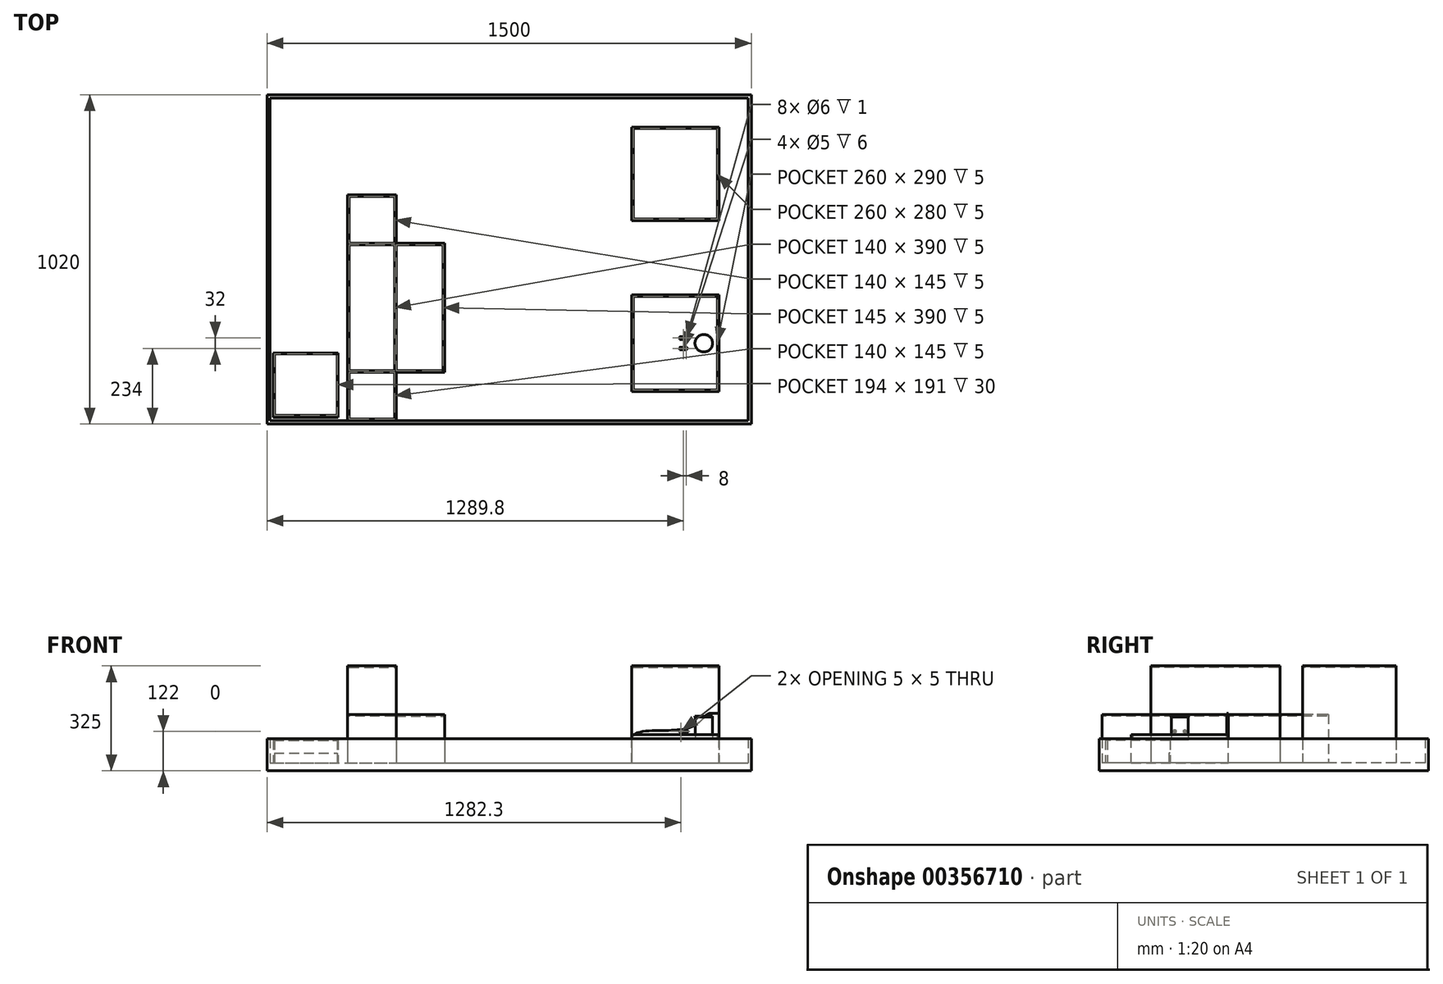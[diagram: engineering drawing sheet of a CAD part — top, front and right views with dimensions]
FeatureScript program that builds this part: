
annotation { "Feature Type Name" : "Feature", "Feature Type Description" : "" }
export const myFeature = defineFeature(function(context is Context, id is Id, definition is map)
    precondition{}
    {
        {
            var Q0;
            Q0=qCreatedBy(makeId("Top.planeOp"),FACE);
            var sketch = newSketch(context, id + "F0", { "sketchPlane" : qUnion([Q0])});
            skCircle(sketch, "E0", {"center": v(0, 0) * mm, "radius": 27.2 * mm});
            skSolve(sketch);
        }
        {
            var Q0;
            Q0=qSketchRegion(id+"F0",true);
            extrude(context, id + "F1", {"entities" : qUnion([Q0]), "depth" : 2.83 * mm});
        }
        {
            var Q0;
            Q0=makeQuery(id+"F1.opExtrude","CAP_FACE",FACE,{"disambiguationData":[OSD([sQuery(id+"F0.wireOp",EDGE,"E0")])],"isStart":false});
            var sketch = newSketch(context, id + "F2", { "sketchPlane" : qUnion([Q0])});
            skCircle(sketch, "E1", {"center": v(0, 0) * mm, "radius": 26.4 * mm});
            skSolve(sketch);
        }
        {
            var Q0;
            Q0=qSketchRegion(id+"F2",true);
            extrude(context, id + "F3", {"entities" : qUnion([Q0]), "operationType" : NewBodyOperationType.ADD, "depth" : 67.36 * mm});
        }
        {
            var Q0;
            Q0=makeQuery(id+"F3.opExtrude","CAP_FACE",FACE,{"disambiguationData":[OSD([sQuery(id+"F2.wireOp",EDGE,"E1")])],"isStart":false});
            var sketch = newSketch(context, id + "F4", { "sketchPlane" : qUnion([Q0])});
            skCircle(sketch, "E2", {"center": v(0, 0) * mm, "radius": 27.2 * mm});
            skSolve(sketch);
        }
        {
            var Q0;
            Q0=qSketchRegion(id+"F4",true);
            extrude(context, id + "F5", {"entities" : qUnion([Q0]), "operationType" : NewBodyOperationType.ADD, "depth" : 2.83 * mm});
        }
        {
            var Q0;
            Q0=makeQuery(id+"F5.opExtrude","CAP_FACE",FACE,{"disambiguationData":[OSD([sQuery(id+"F4.wireOp",EDGE,"E2")])],"isStart":false});
            var sketch = newSketch(context, id + "F6", { "sketchPlane" : qUnion([Q0])});
            skSolve(sketch);
        }
        {
            var Q0;
            Q0=qCreatedBy(makeId("Top.planeOp"),FACE);
            cPlane(context, id + "F7", {"entities" : qUnion([Q0]), "cplaneType" : CPlaneType.OFFSET, "offset" : 25 * mm, "width" : 150 * mm, "height" : 150 * mm});
        }
        {
            var Q0;
            Q0=makeQuery(id+"F6.imprint","IMPRINT",FACE,{"disambiguationData":[TD([[makeQuery(id+"F6.imprint","IMPRINT",EDGE,{"derivedFrom":makeQuery(id+"F5.opExtrude","CAP_EDGE",EDGE,{"disambiguationData":[OSD([sQuery(id+"F4.wireOp",EDGE,"E2")])],"isStart":false})}),1.0]])]});
            var sketch = newSketch(context, id + "F8", { "sketchPlane" : qUnion([Q0])});
            skSolve(sketch);
        }
        {
            var Q0;
            Q0=qCreatedBy(makeId("Top.planeOp"),FACE);
            var sketch = newSketch(context, id + "F9", { "sketchPlane" : qUnion([Q0])});
            skLineSegment(sketch, "E3.bottom", {"start": v(-222.8, -150) * mm, "end": v(47.2, -150) * mm});
            skLineSegment(sketch, "E3.top", {"start": v(-222.8, 150) * mm, "end": v(47.2, 150) * mm});
            skLineSegment(sketch, "E3.left", {"start": v(-222.8, -150) * mm, "end": v(-222.8, 150) * mm});
            skLineSegment(sketch, "E3.right", {"start": v(47.2, -150) * mm, "end": v(47.2, 150) * mm});
            skSolve(sketch);
        }
        {
            var Q0;
            Q0=qSketchRegion(id+"F9",true);
            extrude(context, id + "F10", {"entities" : qUnion([Q0]), "oppositeDirection" : true, "depth" : 72 * mm});
        }
        {
            var Q0;
            Q0=makeQuery(id+"F10.opExtrude","CAP_FACE",FACE,{"disambiguationData":[OSD([sQuery(id+"F9.wireOp",EDGE,"E3.bottom"),sQuery(id+"F9.wireOp",EDGE,"E3.top"),sQuery(id+"F9.wireOp",EDGE,"E3.left"),sQuery(id+"F9.wireOp",EDGE,"E3.right")])],"isStart":true});
            var sketch = newSketch(context, id + "F11", { "sketchPlane" : qUnion([Q0])});
            skLineSegment(sketch, "E4.bottom", {"start": v(-222.8, -150) * mm, "end": v(47.2, -150) * mm});
            skLineSegment(sketch, "E4.top", {"start": v(-222.8, -145) * mm, "end": v(42.2, -145) * mm});
            skLineSegment(sketch, "E4.left", {"start": v(-222.8, -150) * mm, "end": v(-222.8, -145) * mm});
            skLineSegment(sketch, "E5.bottom", {"start": v(47.2, 150) * mm, "end": v(42.2, 150) * mm});
            skLineSegment(sketch, "E5.left", {"start": v(47.2, 150) * mm, "end": v(47.2, -150) * mm});
            skLineSegment(sketch, "E5.right", {"start": v(42.2, 150) * mm, "end": v(42.2, -145) * mm});
            skSolve(sketch);
        }
        {
            var Q0;
            Q0=qSketchRegion(id+"F11",true);
            extrude(context, id + "F12", {"entities" : qUnion([Q0]), "operationType" : NewBodyOperationType.ADD, "depth" : 15 * mm});
        }
        {
            var Q0;
            Q0=makeQuery(id+"F12.boolean.opBoolean","MERGE",FACE,{"derivedFrom":[makeQuery(id+"F10.opExtrude","SWEPT_FACE",FACE,{"disambiguationData":[OSD([sQuery(id+"F9.wireOp",EDGE,"E3.top")])]}),makeQuery(id+"F12.opExtrude","SWEPT_FACE",FACE,{"disambiguationData":[OSD([sQuery(id+"F11.wireOp",EDGE,"E5.bottom")])]})]});
            var sketch = newSketch(context, id + "F13", { "sketchPlane" : qUnion([Q0])});
            skLineSegment(sketch, "E6", {"start": v(-47.2, 81.36) * mm, "end": v(-21.31, 81.36) * mm});
            skFitSpline(sketch, "E7", {"points": [v(-21.31, 81.36) * mm, v(15.24, 52.01) * mm, v(114.14, 28.17) * mm, v(222.8, 0) * mm], "startDerivative": vector(181.02, 0.3) * mm, "endDerivative": vector(-1.73, -239.85) * mm});
            skLineSegment(sketch, "E8", {"start": v(-47.2, 81.36) * mm, "end": v(-47.2, -72) * mm});
            skLineSegment(sketch, "E9", {"start": v(-47.2, -72) * mm, "end": v(222.8, -72) * mm});
            skLineSegment(sketch, "E10", {"start": v(222.8, -72) * mm, "end": v(222.8, 0) * mm});
            skSolve(sketch);
        }
        {
            var Q0;
            Q0=qSketchRegion(id+"F13",true);
            extrude(context, id + "F14", {"entities" : qUnion([Q0]), "operationType" : NewBodyOperationType.ADD, "oppositeDirection" : true, "depth" : 5 * mm});
        }
        {
            var Q0;
            Q0=makeQuery(id+"F10.opExtrude","CAP_FACE",FACE,{"disambiguationData":[OSD([sQuery(id+"F9.wireOp",EDGE,"E3.bottom"),sQuery(id+"F9.wireOp",EDGE,"E3.top"),sQuery(id+"F9.wireOp",EDGE,"E3.left"),sQuery(id+"F9.wireOp",EDGE,"E3.right")])],"isStart":true});
            var sketch = newSketch(context, id + "F15", { "sketchPlane" : qUnion([Q0])});
            skLineSegment(sketch, "E11.bottom", {"start": v(-222.8, 145) * mm, "end": v(-217.8, 145) * mm});
            skLineSegment(sketch, "E11.top", {"start": v(-222.8, -145) * mm, "end": v(-217.8, -145) * mm});
            skLineSegment(sketch, "E11.left", {"start": v(-222.8, 145) * mm, "end": v(-222.8, -145) * mm});
            skLineSegment(sketch, "E11.right", {"start": v(-217.8, 145) * mm, "end": v(-217.8, -145) * mm});
            skSolve(sketch);
        }
        {
            var Q0;
            Q0=qSketchRegion(id+"F15",true);
            extrude(context, id + "F16", {"entities" : qUnion([Q0]), "operationType" : NewBodyOperationType.ADD, "depth" : 5 * mm});
        }
        {
            var Q0;
            Q0=makeQuery(id+"F10.opExtrude","CAP_FACE",FACE,{"disambiguationData":[OSD([sQuery(id+"F9.wireOp",EDGE,"E3.bottom"),sQuery(id+"F9.wireOp",EDGE,"E3.top"),sQuery(id+"F9.wireOp",EDGE,"E3.left"),sQuery(id+"F9.wireOp",EDGE,"E3.right")])],"isStart":false});
            var sketch = newSketch(context, id + "F17", { "sketchPlane" : qUnion([Q0])});
            skLineSegment(sketch, "E12.bottom", {"start": v(147.2, 250) * mm, "end": v(-1352.8, 250) * mm});
            skLineSegment(sketch, "E12.top", {"start": v(147.2, -770) * mm, "end": v(-1352.8, -770) * mm});
            skLineSegment(sketch, "E12.left", {"start": v(147.2, 250) * mm, "end": v(147.2, -770) * mm});
            skLineSegment(sketch, "E12.right", {"start": v(-1352.8, 250) * mm, "end": v(-1352.8, -770) * mm});
            skSolve(sketch);
        }
        {
            var Q0;
            Q0=qSketchRegion(id+"F17",true);
            extrude(context, id + "F18", {"entities" : qUnion([Q0]), "operationType" : NewBodyOperationType.ADD, "depth" : 25 * mm});
        }
        {
            var Q0;
            Q0=makeQuery(id+"F18.opExtrude","CAP_FACE",FACE,{"disambiguationData":[OSD([sQuery(id+"F17.wireOp",EDGE,"E12.bottom"),sQuery(id+"F17.wireOp",EDGE,"E12.top"),sQuery(id+"F17.wireOp",EDGE,"E12.left"),sQuery(id+"F17.wireOp",EDGE,"E12.right")])],"isStart":true});
            var sketch = newSketch(context, id + "F19", { "sketchPlane" : qUnion([Q0])});
            skLineSegment(sketch, "E13.bottom", {"start": v(-222.8, 670) * mm, "end": v(47.2, 670) * mm});
            skLineSegment(sketch, "E13.top", {"start": v(-222.8, 380) * mm, "end": v(47.2, 380) * mm});
            skLineSegment(sketch, "E13.left", {"start": v(-222.8, 670) * mm, "end": v(-222.8, 380) * mm});
            skLineSegment(sketch, "E13.right", {"start": v(47.2, 670) * mm, "end": v(47.2, 380) * mm});
            skSolve(sketch);
        }
        {
            var Q0;
            Q0=qSketchRegion(id+"F19",true);
            extrude(context, id + "F20", {"entities" : qUnion([Q0]), "operationType" : NewBodyOperationType.ADD, "depth" : 300 * mm});
        }
        {
            var Q0;
            Q0=makeQuery(id+"F20.opExtrude","CAP_FACE",FACE,{"disambiguationData":[OSD([sQuery(id+"F19.wireOp",EDGE,"E13.bottom"),sQuery(id+"F19.wireOp",EDGE,"E13.top"),sQuery(id+"F19.wireOp",EDGE,"E13.left"),sQuery(id+"F19.wireOp",EDGE,"E13.right")])],"isStart":false});
            var sketch = newSketch(context, id + "F21", { "sketchPlane" : qUnion([Q0])});
            skLineSegment(sketch, "E14.bottom", {"start": v(-217.8, 665) * mm, "end": v(42.2, 665) * mm});
            skLineSegment(sketch, "E14.top", {"start": v(-217.8, 385) * mm, "end": v(42.2, 385) * mm});
            skLineSegment(sketch, "E14.left", {"start": v(-217.8, 665) * mm, "end": v(-217.8, 385) * mm});
            skLineSegment(sketch, "E14.right", {"start": v(42.2, 665) * mm, "end": v(42.2, 385) * mm});
            skSolve(sketch);
        }
        {
            var Q0;
            Q0=qSketchRegion(id+"F21",true);
            extrude(context, id + "F22", {"entities" : qUnion([Q0]), "operationType" : NewBodyOperationType.REMOVE, "oppositeDirection" : true, "depth" : 5 * mm});
        }
        {
            var Q0;
            Q0=makeQuery(id+"F18.opExtrude","CAP_FACE",FACE,{"disambiguationData":[OSD([sQuery(id+"F17.wireOp",EDGE,"E12.bottom"),sQuery(id+"F17.wireOp",EDGE,"E12.top"),sQuery(id+"F17.wireOp",EDGE,"E12.left"),sQuery(id+"F17.wireOp",EDGE,"E12.right")])],"isStart":true});
            var sketch = newSketch(context, id + "F23", { "sketchPlane" : qUnion([Q0])});
            skLineSegment(sketch, "E15.bottom", {"start": v(-1352.8, 770) * mm, "end": v(147.2, 770) * mm});
            skLineSegment(sketch, "E15.top", {"start": v(-1352.8, -250) * mm, "end": v(147.2, -250) * mm});
            skLineSegment(sketch, "E15.left", {"start": v(-1352.8, 770) * mm, "end": v(-1352.8, -250) * mm});
            skLineSegment(sketch, "E15.right", {"start": v(147.2, 770) * mm, "end": v(147.2, -250) * mm});
            skLineSegment(sketch, "E16.bottom", {"start": v(-1342.8, 760) * mm, "end": v(137.2, 760) * mm});
            skLineSegment(sketch, "E16.top", {"start": v(-1342.8, -240) * mm, "end": v(137.2, -240) * mm});
            skLineSegment(sketch, "E16.left", {"start": v(-1342.8, 760) * mm, "end": v(-1342.8, -240) * mm});
            skLineSegment(sketch, "E16.right", {"start": v(137.2, 760) * mm, "end": v(137.2, -240) * mm});
            skSolve(sketch);
        }
        {
            var Q0;
            Q0=qSketchRegion(id+"F23",true);
            extrude(context, id + "F24", {"entities" : qUnion([Q0]), "operationType" : NewBodyOperationType.ADD, "depth" : 75 * mm});
        }
        {
            var Q0;
            Q0=makeQuery(id+"F18.opExtrude","CAP_FACE",FACE,{"disambiguationData":[OSD([sQuery(id+"F17.wireOp",EDGE,"E12.bottom"),sQuery(id+"F17.wireOp",EDGE,"E12.top"),sQuery(id+"F17.wireOp",EDGE,"E12.left"),sQuery(id+"F17.wireOp",EDGE,"E12.right")])],"isStart":true});
            var sketch = newSketch(context, id + "F25", { "sketchPlane" : qUnion([Q0])});
            skLineSegment(sketch, "E17.bottom", {"start": v(-1102.8, 460) * mm, "end": v(-952.8, 460) * mm});
            skLineSegment(sketch, "E17.top", {"start": v(-1102.8, -240) * mm, "end": v(-952.8, -240) * mm});
            skLineSegment(sketch, "E17.left", {"start": v(-1102.8, 460) * mm, "end": v(-1102.8, -240) * mm});
            skLineSegment(sketch, "E17.right", {"start": v(-952.8, 460) * mm, "end": v(-952.8, 310) * mm});
            skLineSegment(sketch, "E18.bottom", {"start": v(-952.8, 310) * mm, "end": v(-802.8, 310) * mm});
            skLineSegment(sketch, "E18.top", {"start": v(-952.8, -90) * mm, "end": v(-802.8, -90) * mm});
            skLineSegment(sketch, "E18.right", {"start": v(-802.8, 310) * mm, "end": v(-802.8, -90) * mm});
            skLineSegment(sketch, "E19.trimOffspring", {"start": v(-952.8, -90) * mm, "end": v(-952.8, -240) * mm});
            skSolve(sketch);
        }
        {
            var Q0;
            Q0=qSketchRegion(id+"F25",true);
            extrude(context, id + "F26", {"entities" : qUnion([Q0]), "operationType" : NewBodyOperationType.ADD, "depth" : 150 * mm});
        }
        {
            var Q0;
            Q0=makeQuery(id+"F26.opExtrude","CAP_FACE",FACE,{"disambiguationData":[OSD([sQuery(id+"F25.wireOp",EDGE,"E17.bottom"),sQuery(id+"F25.wireOp",EDGE,"E17.top"),sQuery(id+"F25.wireOp",EDGE,"E17.left"),sQuery(id+"F25.wireOp",EDGE,"E17.right"),sQuery(id+"F25.wireOp",EDGE,"E18.bottom"),sQuery(id+"F25.wireOp",EDGE,"E18.top"),sQuery(id+"F25.wireOp",EDGE,"E18.right"),sQuery(id+"F25.wireOp",EDGE,"E19.trimOffspring")])],"isStart":false});
            var sketch = newSketch(context, id + "F27", { "sketchPlane" : qUnion([Q0])});
            skLineSegment(sketch, "E20.bottom", {"start": v(-952.8, 310) * mm, "end": v(-1102.8, 310) * mm});
            skLineSegment(sketch, "E20.top", {"start": v(-952.8, -90) * mm, "end": v(-1102.8, -90) * mm});
            skLineSegment(sketch, "E20.left", {"start": v(-952.8, 310) * mm, "end": v(-952.8, -90) * mm});
            skLineSegment(sketch, "E20.right", {"start": v(-1102.8, 310) * mm, "end": v(-1102.8, -90) * mm});
            skSolve(sketch);
        }
        {
            var Q0;
            Q0=qSketchRegion(id+"F27",true);
            extrude(context, id + "F28", {"entities" : qUnion([Q0]), "operationType" : NewBodyOperationType.ADD, "depth" : 150 * mm});
        }
        {
            var Q0;
            Q0=makeQuery(id+"F28.opExtrude","CAP_FACE",FACE,{"disambiguationData":[OSD([sQuery(id+"F27.wireOp",EDGE,"E20.bottom"),sQuery(id+"F27.wireOp",EDGE,"E20.top"),sQuery(id+"F27.wireOp",EDGE,"E20.left"),sQuery(id+"F27.wireOp",EDGE,"E20.right")])],"isStart":false});
            var sketch = newSketch(context, id + "F29", { "sketchPlane" : qUnion([Q0])});
            skLineSegment(sketch, "E21.bottom", {"start": v(-1097.8, 305) * mm, "end": v(-957.8, 305) * mm});
            skLineSegment(sketch, "E21.top", {"start": v(-1097.8, -85) * mm, "end": v(-957.8, -85) * mm});
            skLineSegment(sketch, "E21.left", {"start": v(-1097.8, 305) * mm, "end": v(-1097.8, -85) * mm});
            skLineSegment(sketch, "E21.right", {"start": v(-957.8, 305) * mm, "end": v(-957.8, -85) * mm});
            skSolve(sketch);
        }
        {
            var Q0;
            Q0=qSketchRegion(id+"F29",true);
            extrude(context, id + "F30", {"entities" : qUnion([Q0]), "operationType" : NewBodyOperationType.REMOVE, "oppositeDirection" : true, "depth" : 5 * mm});
        }
        {
            var Q0;
            {var subQ0=sQuery(id+"F25.wireOp",EDGE,"E17.left");var subQ1=sQuery(id+"F25.wireOp",EDGE,"E18.bottom");var subQ2=sQuery(id+"F25.wireOp",EDGE,"E17.right");var subQ3=sQuery(id+"F25.wireOp",EDGE,"E17.bottom");var subQ4=makeQuery(id+"F26.opExtrude","CAP_FACE",FACE,{"disambiguationData":[OSD([subQ3,sQuery(id+"F25.wireOp",EDGE,"E17.top"),subQ0,subQ2,subQ1,sQuery(id+"F25.wireOp",EDGE,"E18.top"),sQuery(id+"F25.wireOp",EDGE,"E18.right"),sQuery(id+"F25.wireOp",EDGE,"E19.trimOffspring")])],"isStart":false});Q0=makeQuery(id+"F28.boolean.opBoolean","SPLIT",FACE,{"disambiguationData":[TD([makeQuery(id+"F26.opExtrude","SWEPT_FACE",FACE,{"disambiguationData":[OSD([subQ3])]})])],"derivedFrom":subQ4});}
            var sketch = newSketch(context, id + "F31", { "sketchPlane" : qUnion([Q0])});
            skLineSegment(sketch, "E22.bottom", {"start": v(-1097.8, 455) * mm, "end": v(-957.8, 455) * mm});
            skLineSegment(sketch, "E22.top", {"start": v(-1097.8, 310) * mm, "end": v(-957.8, 310) * mm});
            skLineSegment(sketch, "E22.left", {"start": v(-1097.8, 455) * mm, "end": v(-1097.8, 310) * mm});
            skLineSegment(sketch, "E22.right", {"start": v(-957.8, 455) * mm, "end": v(-957.8, 310) * mm});
            skLineSegment(sketch, "E23.bottom", {"start": v(-952.8, 305) * mm, "end": v(-807.8, 305) * mm});
            skLineSegment(sketch, "E23.top", {"start": v(-952.8, -85) * mm, "end": v(-807.8, -85) * mm});
            skLineSegment(sketch, "E23.left", {"start": v(-952.8, 305) * mm, "end": v(-952.8, -85) * mm});
            skLineSegment(sketch, "E23.right", {"start": v(-807.8, 305) * mm, "end": v(-807.8, -85) * mm});
            skLineSegment(sketch, "E24.bottom", {"start": v(-1097.8, -90) * mm, "end": v(-957.8, -90) * mm});
            skLineSegment(sketch, "E24.top", {"start": v(-1097.8, -235) * mm, "end": v(-957.8, -235) * mm});
            skLineSegment(sketch, "E24.left", {"start": v(-1097.8, -90) * mm, "end": v(-1097.8, -235) * mm});
            skLineSegment(sketch, "E24.right", {"start": v(-957.8, -90) * mm, "end": v(-957.8, -235) * mm});
            skSolve(sketch);
        }
        {
            var Q0;
            Q0=qSketchRegion(id+"F31",true);
            extrude(context, id + "F32", {"entities" : qUnion([Q0]), "operationType" : NewBodyOperationType.REMOVE, "oppositeDirection" : true, "depth" : 5 * mm});
        }
        {
            var Q0;
            Q0=qCreatedBy(id+"F7.planeOp",FACE);
            var sketch = newSketch(context, id + "F33", { "sketchPlane" : qUnion([Q0])});
            skLineSegment(sketch, "E25", {"start": v(0, 0) * mm, "end": v(-90, 0) * mm, "construction": true});
            skLineSegment(sketch, "E26.bottom", {"start": v(-74.5, -12) * mm, "end": v(-55, -12) * mm});
            skLineSegment(sketch, "E26.top", {"start": v(-74.5, -20) * mm, "end": v(-55, -20) * mm});
            skLineSegment(sketch, "E26.left", {"start": v(-74.5, -12) * mm, "end": v(-74.5, -13) * mm});
            skPoint(sketch, "E27.visualSharp", {"position": v(-51, -12) * mm});
            skPoint(sketch, "E28.visualSharp", {"position": v(-51, -20) * mm});
            skCircle(sketch, "E29", {"center": v(-55, -16) * mm, "radius": 3 * mm});
            skLineSegment(sketch, "E30", {"start": v(-59, -3.98) * mm, "end": v(-59, -18.08) * mm, "construction": true});
            skCircle(sketch, "E31.MirrorC", {"center": v(-63, -16) * mm, "radius": 3 * mm});
            skLineSegment(sketch, "E32.bottom", {"start": v(-74.5, -13) * mm, "end": v(-65.65, -13) * mm});
            skLineSegment(sketch, "E32.top", {"start": v(-74.5, -19) * mm, "end": v(-65.65, -19) * mm});
            skArc(sketch, "E33", {"start": v(-65.65, -13) * mm, "mid": v(-67, -16) * mm, "end": v(-65.65, -19) * mm});
            skLineSegment(sketch, "E34.trimOffspring", {"start": v(-74.5, -19) * mm, "end": v(-74.5, -20) * mm});
            skArc(sketch, "E35.trimOffspring", {"start": v(-55, -20) * mm, "mid": v(-51, -16) * mm, "end": v(-55, -12) * mm});
            skLineSegment(sketch, "E36.MirrorCS", {"start": v(-74.5, 12) * mm, "end": v(-74.5, 13) * mm});
            skLineSegment(sketch, "E37.MirrorCS", {"start": v(-74.5, 19) * mm, "end": v(-74.5, 20) * mm});
            skPoint(sketch, "E38.MirrorP", {"position": v(-51, 12) * mm});
            skLineSegment(sketch, "E39.MirrorCS", {"start": v(-74.5, 12) * mm, "end": v(-55, 12) * mm});
            skPoint(sketch, "E40.MirrorP", {"position": v(-51, 20) * mm});
            skArc(sketch, "E41.MirrorCS", {"start": v(-65.65, 13) * mm, "mid": v(-67, 16) * mm, "end": v(-65.65, 19) * mm});
            skArc(sketch, "E42.MirrorCS", {"start": v(-55, 20) * mm, "mid": v(-51, 16) * mm, "end": v(-55, 12) * mm});
            skLineSegment(sketch, "E43.MirrorCS", {"start": v(-74.5, 20) * mm, "end": v(-55, 20) * mm});
            skCircle(sketch, "E44.MirrorC", {"center": v(-55, 16) * mm, "radius": 3 * mm});
            skCircle(sketch, "E45.MirrorC", {"center": v(-63, 16) * mm, "radius": 3 * mm});
            skLineSegment(sketch, "E46.MirrorCS", {"start": v(-74.5, 19) * mm, "end": v(-65.65, 19) * mm});
            skLineSegment(sketch, "E47.MirrorCS", {"start": v(-74.5, 13) * mm, "end": v(-65.65, 13) * mm});
            skSolve(sketch);
        }
        {
            var Q0;
            Q0=qSketchRegion(id+"F33",true);
            var Q1;
            Q1=qSketchRegion(id+"F36",true);
            extrude(context, id + "F34", {"entities" : qUnion([Q0, Q1]), "depth" : 8 * mm, "symmetric" : true});
        }
        {
            var Q0;
            Q0=makeQuery(id+"F34.opExtrude","CAP_EDGE",EDGE,{"disambiguationData":[OSD([sQuery(id+"F33.wireOp",EDGE,"E34.trimOffspring")])],"isStart":false});
            var Q1;
            Q1=makeQuery(id+"F34.opExtrude","CAP_EDGE",EDGE,{"disambiguationData":[OSD([sQuery(id+"F33.wireOp",EDGE,"E26.left")])],"isStart":false});
            var Q2;
            Q2=makeQuery(id+"F34.opExtrude","CAP_EDGE",EDGE,{"disambiguationData":[OSD([sQuery(id+"F33.wireOp",EDGE,"E34.trimOffspring")])],"isStart":true});
            var Q3;
            Q3=makeQuery(id+"F34.opExtrude","CAP_EDGE",EDGE,{"disambiguationData":[OSD([sQuery(id+"F33.wireOp",EDGE,"E26.left")])],"isStart":true});
            var Q4;
            Q4=makeQuery(id+"F34.opExtrude","CAP_EDGE",EDGE,{"disambiguationData":[OSD([sQuery(id+"F33.wireOp",EDGE,"E36.MirrorCS")])],"isStart":false});
            var Q5;
            Q5=makeQuery(id+"F34.opExtrude","CAP_EDGE",EDGE,{"disambiguationData":[OSD([sQuery(id+"F33.wireOp",EDGE,"E37.MirrorCS")])],"isStart":false});
            var Q6;
            Q6=makeQuery(id+"F34.opExtrude","CAP_EDGE",EDGE,{"disambiguationData":[OSD([sQuery(id+"F33.wireOp",EDGE,"E37.MirrorCS")])],"isStart":true});
            var Q7;
            Q7=makeQuery(id+"F34.opExtrude","CAP_EDGE",EDGE,{"disambiguationData":[OSD([sQuery(id+"F33.wireOp",EDGE,"E36.MirrorCS")])],"isStart":true});
            fillet(context, id + "F35", {"entities" : qUnion([Q0, Q1, Q2, Q3, Q4, Q5, Q6, Q7]), "radius" : 4 * mm, "tangentPropagation" : true, "allowEdgeOverflow" : false});
        }
        {
            var Q0;
            Q0=makeQuery(id+"F34.opExtrude","SWEPT_FACE",FACE,{"disambiguationData":[OSD([sQuery(id+"F33.wireOp",EDGE,"E26.top")])]});
            var sketch = newSketch(context, id + "F36", { "sketchPlane" : qUnion([Q0])});
            skCircle(sketch, "E48", {"center": v(-70.5, 25) * mm, "radius": 3 * mm});
            skSolve(sketch);
        }
        {
            var Q0;
            Q0=qSketchRegion(id+"F36",true);
            var Q1;
            Q1=makeQuery(id+"F34.opExtrude","SWEPT_FACE",FACE,{"disambiguationData":[OSD([sQuery(id+"F33.wireOp",EDGE,"E26.bottom")])]});
            extrude(context, id + "F37", {"entities" : qUnion([Q0]), "operationType" : NewBodyOperationType.ADD, "endBound" : BoundingType.UP_TO_SURFACE, "oppositeDirection" : true, "endBoundEntityFace" : qUnion([Q1]), "depth" : 25 * mm});
        }
        {
            var Q0;
            Q0=makeQuery(id+"F34.opExtrude","SWEPT_FACE",FACE,{"disambiguationData":[OSD([sQuery(id+"F33.wireOp",EDGE,"E43.MirrorCS")])]});
            var sketch = newSketch(context, id + "F38", { "sketchPlane" : qUnion([Q0])});
            skCircle(sketch, "E49", {"center": v(70.5, 25) * mm, "radius": 3 * mm});
            skSolve(sketch);
        }
        {
            var Q0;
            Q0=qSketchRegion(id+"F38",true);
            var Q1;
            Q1=makeQuery(id+"F34.opExtrude","SWEPT_FACE",FACE,{"disambiguationData":[OSD([sQuery(id+"F33.wireOp",EDGE,"E39.MirrorCS")])]});
            extrude(context, id + "F39", {"entities" : qUnion([Q0]), "operationType" : NewBodyOperationType.ADD, "endBound" : BoundingType.UP_TO_SURFACE, "oppositeDirection" : true, "endBoundEntityFace" : qUnion([Q1]), "depth" : 25 * mm});
        }
        {
            var Q0;
            Q0=qCreatedBy(id+"F7.planeOp",FACE);
            var sketch = newSketch(context, id + "F40", { "sketchPlane" : qUnion([Q0])});
            skCircle(sketch, "E50", {"center": v(-55, 16) * mm, "radius": 3 * mm});
            skCircle(sketch, "E51", {"center": v(-63, 16) * mm, "radius": 2.5 * mm});
            skCircle(sketch, "E52", {"center": v(-63, 16) * mm, "radius": 3 * mm});
            skCircle(sketch, "E53", {"center": v(-55, 16) * mm, "radius": 2.5 * mm});
            skSolve(sketch);
        }
        {
            var Q0;
            Q0=qSketchRegion(id+"F40",true);
            extrude(context, id + "F41", {"entities" : qUnion([Q0]), "operationType" : NewBodyOperationType.ADD, "depth" : 6 * mm, "symmetric" : true});
        }
        {
            var Q0;
            Q0=qCreatedBy(id+"F7.planeOp",FACE);
            var sketch = newSketch(context, id + "F42", { "sketchPlane" : qUnion([Q0])});
            skCircle(sketch, "E54", {"center": v(-63, -16) * mm, "radius": 2.5 * mm});
            skCircle(sketch, "E55", {"center": v(-63, -16) * mm, "radius": 3 * mm});
            skCircle(sketch, "E56", {"center": v(-55, -16) * mm, "radius": 2.5 * mm});
            skCircle(sketch, "E57", {"center": v(-55, -16) * mm, "radius": 3 * mm});
            skSolve(sketch);
        }
        {
            var Q0;
            Q0=qSketchRegion(id+"F42",true);
            extrude(context, id + "F43", {"entities" : qUnion([Q0]), "operationType" : NewBodyOperationType.ADD, "depth" : 6 * mm, "symmetric" : true});
        }
        {
            var Q0;
            Q0=makeQuery(id+"F34.opExtrude","SWEPT_FACE",FACE,{"disambiguationData":[OSD([sQuery(id+"F33.wireOp",EDGE,"E43.MirrorCS")])]});
            var sketch = newSketch(context, id + "F44", { "sketchPlane" : qUnion([Q0])});
            skArc(sketch, "E58", {"start": v(71.5, 27.3) * mm, "mid": v(70.5, 27.5) * mm, "end": v(69.5, 27.3) * mm});
            skLineSegment(sketch, "E59.bottom", {"start": v(68.2, 26) * mm, "end": v(69.5, 26) * mm});
            skLineSegment(sketch, "E59.top", {"start": v(68.2, 24) * mm, "end": v(69.5, 24) * mm});
            skLineSegment(sketch, "E60.left", {"start": v(71.5, 27.3) * mm, "end": v(71.5, 26) * mm});
            skLineSegment(sketch, "E60.right", {"start": v(69.5, 27.3) * mm, "end": v(69.5, 26) * mm});
            skPoint(sketch, "E61.orphan", {"position": v(69.5, 27.8) * mm});
            skPoint(sketch, "E62.orphan", {"position": v(71.5, 27.8) * mm});
            skArc(sketch, "E63.trimOffspring", {"start": v(68.2, 26) * mm, "mid": v(68, 25) * mm, "end": v(68.2, 24) * mm});
            skPoint(sketch, "E59.left.start.orphan", {"position": v(67.32, 26) * mm});
            skPoint(sketch, "E64.orphan", {"position": v(67.32, 24) * mm});
            skArc(sketch, "E65.trimOffspring", {"start": v(69.5, 22.7) * mm, "mid": v(70.5, 22.5) * mm, "end": v(71.5, 22.7) * mm});
            skLineSegment(sketch, "E66.trimOffspring", {"start": v(69.5, 24) * mm, "end": v(69.5, 22.7) * mm});
            skLineSegment(sketch, "E67.trimOffspring", {"start": v(71.5, 26) * mm, "end": v(72.8, 26) * mm});
            skLineSegment(sketch, "E68.trimOffspring", {"start": v(71.5, 24) * mm, "end": v(71.5, 22.7) * mm});
            skLineSegment(sketch, "E69.trimOffspring", {"start": v(71.5, 24) * mm, "end": v(72.8, 24) * mm});
            skPoint(sketch, "E60.top.end.orphan", {"position": v(69.5, 22.2) * mm});
            skPoint(sketch, "E70.orphan", {"position": v(71.5, 22.2) * mm});
            skPoint(sketch, "E59.right.end.orphan", {"position": v(73.68, 24) * mm});
            skPoint(sketch, "E71.orphan", {"position": v(73.68, 26) * mm});
            skArc(sketch, "E72.trimOffspring", {"start": v(72.8, 24) * mm, "mid": v(73, 25) * mm, "end": v(72.8, 26) * mm});
            skSolve(sketch);
        }
        {
            var Q0;
            Q0=qSketchRegion(id+"F44",true);
            extrude(context, id + "F45", {"entities" : qUnion([Q0]), "operationType" : NewBodyOperationType.REMOVE, "endBound" : BoundingType.THROUGH_ALL, "oppositeDirection" : true, "depth" : 25 * mm});
        }
        {
            var Q0;
            Q0=makeQuery(id+"F18.opExtrude","CAP_FACE",FACE,{"disambiguationData":[OSD([sQuery(id+"F17.wireOp",EDGE,"E12.bottom"),sQuery(id+"F17.wireOp",EDGE,"E12.top"),sQuery(id+"F17.wireOp",EDGE,"E12.left"),sQuery(id+"F17.wireOp",EDGE,"E12.right")])],"isStart":true});
            var sketch = newSketch(context, id + "F46", { "sketchPlane" : qUnion([Q0])});
            skLineSegment(sketch, "E73.bottom", {"start": v(-1332.8, -30) * mm, "end": v(-1132.8, -30) * mm});
            skLineSegment(sketch, "E73.top", {"start": v(-1332.8, -230) * mm, "end": v(-1132.8, -230) * mm});
            skLineSegment(sketch, "E73.left", {"start": v(-1332.8, -30) * mm, "end": v(-1332.8, -230) * mm});
            skLineSegment(sketch, "E73.right", {"start": v(-1132.8, -30) * mm, "end": v(-1132.8, -230) * mm});
            skLineSegment(sketch, "E74.bottom", {"start": v(-1329.8, -33) * mm, "end": v(-1135.8, -33) * mm});
            skLineSegment(sketch, "E74.top", {"start": v(-1329.8, -224) * mm, "end": v(-1135.8, -224) * mm});
            skLineSegment(sketch, "E74.left", {"start": v(-1329.8, -33) * mm, "end": v(-1329.8, -224) * mm});
            skLineSegment(sketch, "E74.right", {"start": v(-1135.8, -33) * mm, "end": v(-1135.8, -224) * mm});
            skSolve(sketch);
        }
        {
            var Q0;
            Q0=qSketchRegion(id+"F46",true);
            extrude(context, id + "F47", {"entities" : qUnion([Q0]), "operationType" : NewBodyOperationType.ADD, "depth" : 30 * mm});
        }
        {
            var Q0;
            Q0=makeQuery(id+"F47.opExtrude","CAP_FACE",FACE,{"disambiguationData":[OSD([sQuery(id+"F46.wireOp",EDGE,"E73.bottom"),sQuery(id+"F46.wireOp",EDGE,"E73.top"),sQuery(id+"F46.wireOp",EDGE,"E73.left"),sQuery(id+"F46.wireOp",EDGE,"E73.right"),sQuery(id+"F46.wireOp",EDGE,"E74.bottom"),sQuery(id+"F46.wireOp",EDGE,"E74.top"),sQuery(id+"F46.wireOp",EDGE,"E74.left"),sQuery(id+"F46.wireOp",EDGE,"E74.right")])],"isStart":false});
            var sketch = newSketch(context, id + "F48", { "sketchPlane" : qUnion([Q0])});
            skLineSegment(sketch, "E75.bottom", {"start": v(-1332.8, -30) * mm, "end": v(-1329.8, -30) * mm});
            skLineSegment(sketch, "E75.top", {"start": v(-1332.8, -230) * mm, "end": v(-1329.8, -230) * mm});
            skLineSegment(sketch, "E75.left", {"start": v(-1332.8, -30) * mm, "end": v(-1332.8, -230) * mm});
            skLineSegment(sketch, "E75.right", {"start": v(-1329.8, -30) * mm, "end": v(-1329.8, -224) * mm});
            skLineSegment(sketch, "E76.bottom", {"start": v(-1329.8, -230) * mm, "end": v(-1135.8, -230) * mm});
            skLineSegment(sketch, "E76.top", {"start": v(-1329.8, -224) * mm, "end": v(-1135.8, -224) * mm});
            skLineSegment(sketch, "E77.bottom", {"start": v(-1135.8, -230) * mm, "end": v(-1132.8, -230) * mm});
            skLineSegment(sketch, "E77.top", {"start": v(-1135.8, -30) * mm, "end": v(-1132.8, -30) * mm});
            skLineSegment(sketch, "E77.left", {"start": v(-1135.8, -224) * mm, "end": v(-1135.8, -30) * mm});
            skLineSegment(sketch, "E77.right", {"start": v(-1132.8, -230) * mm, "end": v(-1132.8, -30) * mm});
            skSolve(sketch);
        }
        {
            var Q0;
            Q0=qSketchRegion(id+"F48",true);
            extrude(context, id + "F49", {"entities" : qUnion([Q0]), "operationType" : NewBodyOperationType.ADD, "depth" : 40 * mm});
        }
    });
